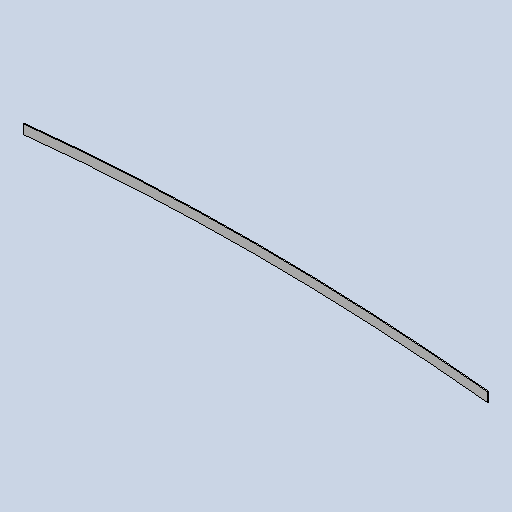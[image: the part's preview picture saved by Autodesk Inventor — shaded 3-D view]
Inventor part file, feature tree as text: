
AUTODESK INVENTOR PART (.ipt)
format: ipt  version: 2025 (Build 290162010, 162A)  size: 326,144 bytes
history: native  units: mm
features: other x2, sheet_metal_op x1, sketch x1
ambient origin geometry x8: Origin, YZ Plane, XZ Plane, XY Plane, X Axis, Y Axis, Z Axis, Center Point
bodies: Body1 (feature_tree)
feature tree (4):
  sheet_metal_op  "Face1"
  sketch  "Sketch5"  dims[d21=8688.265625mm d30=7200.0mm d31=30.0mm d32=1500.0mm d33=3.0mm]
  other  "Plate2"
  other  "Definition1"
